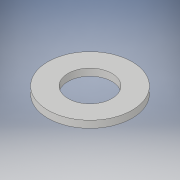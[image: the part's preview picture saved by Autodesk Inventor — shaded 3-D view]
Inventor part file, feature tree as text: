
AUTODESK INVENTOR PART (.ipt)
format: ipt  version: 2019 (Build 230136000, 136)  size: 97,280 bytes
history: native  units: in
note: dims shown in document units (in); Inventor stores cm internally (conversion verified against a paired STEP export)
features: extrude x1, sketch x1
ambient origin geometry x8: Origin, YZ Plane, XZ Plane, XY Plane, X Axis, Y Axis, Z Axis, Center Point
bodies: Solid1 (feature_tree)
feature tree (2):
  extrude  "Extrusion1"  Depth=0.1in
  sketch  "Sketch1"  dims[d0=0.625in d1=1.2in d2=0.1in d3=0.0in]
